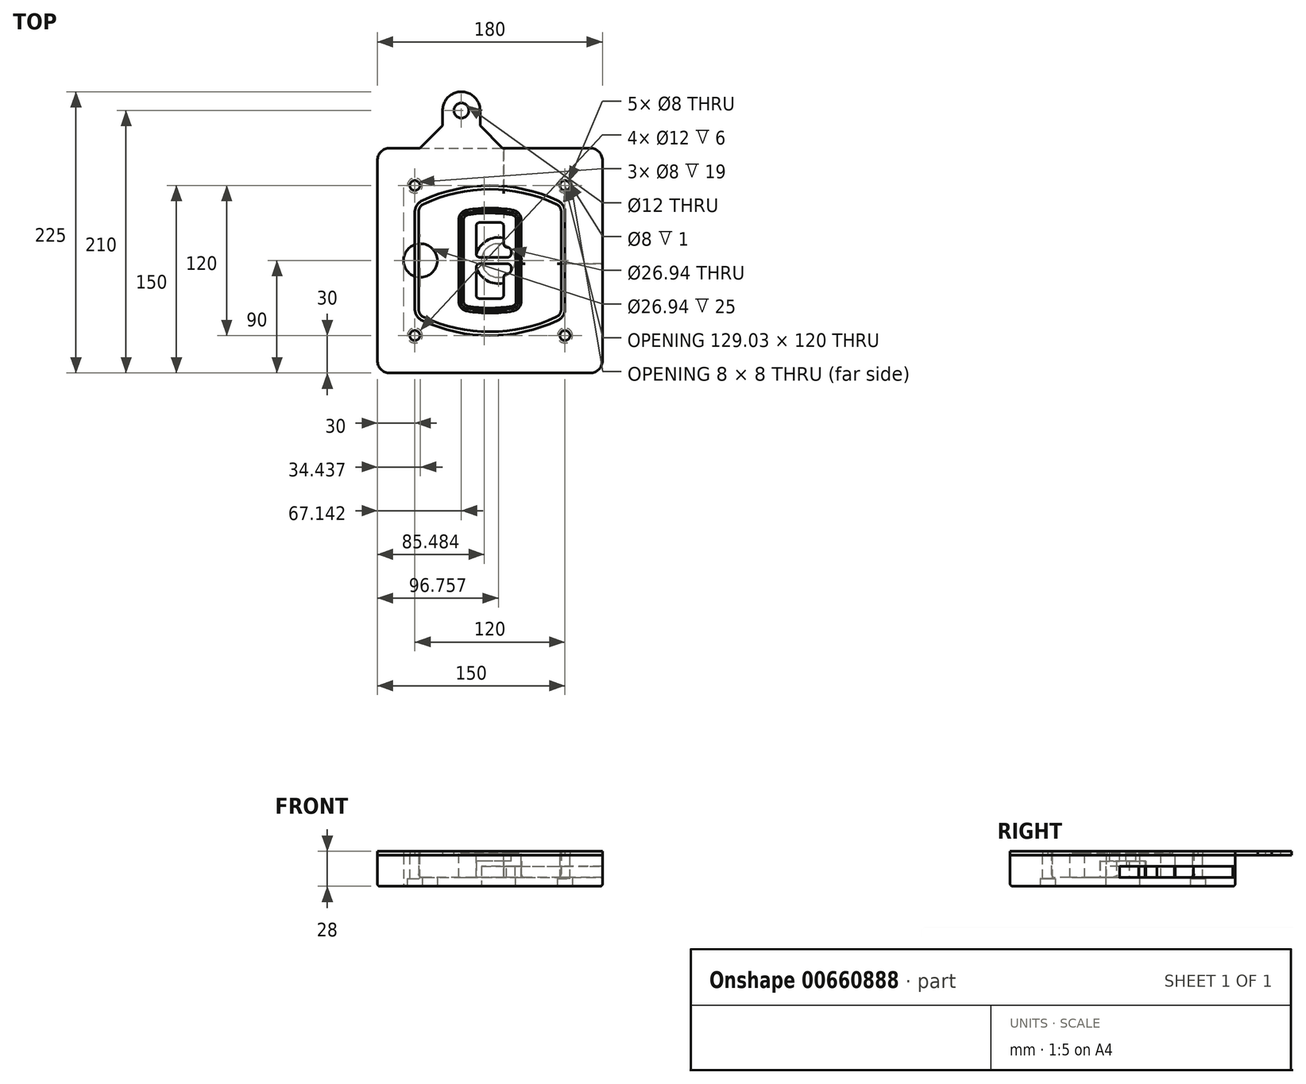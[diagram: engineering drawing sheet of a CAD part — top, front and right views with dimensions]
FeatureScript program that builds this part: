
annotation { "Feature Type Name" : "Feature", "Feature Type Description" : "" }
export const myFeature = defineFeature(function(context is Context, id is Id, definition is map)
    precondition{}
    {
        {
            var Q0;
            Q0=qCreatedBy(makeId("Top.planeOp"),FACE);
            var sketch = newSketch(context, id + "F0", { "sketchPlane" : qUnion([Q0])});
            skPoint(sketch, "E0.rect.middle", {"position": v(0, 0) * mm});
            skLineSegment(sketch, "E1.bottom", {"start": v(-80, -90) * mm, "end": v(80, -90) * mm});
            skLineSegment(sketch, "E1.top", {"start": v(-80, 90) * mm, "end": v(80, 90) * mm});
            skLineSegment(sketch, "E1.left", {"start": v(-90, -80) * mm, "end": v(-90, 80) * mm});
            skLineSegment(sketch, "E1.right", {"start": v(90, -80) * mm, "end": v(90, 80) * mm});
            skLineSegment(sketch, "E2", {"start": v(-90, 90) * mm, "end": v(90, -90) * mm, "construction": true});
            skLineSegment(sketch, "E3", {"start": v(90, 90) * mm, "end": v(-90, -90) * mm, "construction": true});
            skCircle(sketch, "E4", {"center": v(-60, 60) * mm, "radius": 4 * mm});
            skCircle(sketch, "E5", {"center": v(60, 60) * mm, "radius": 4 * mm});
            skCircle(sketch, "E6", {"center": v(60, -60) * mm, "radius": 4 * mm});
            skCircle(sketch, "E7", {"center": v(-60, -60) * mm, "radius": 4 * mm});
            skLineSegment(sketch, "E8", {"start": v(-60, 60) * mm, "end": v(60, 60) * mm, "construction": true});
            skLineSegment(sketch, "E9", {"start": v(60, 60) * mm, "end": v(60, -60) * mm, "construction": true});
            skLineSegment(sketch, "E10", {"start": v(60, -60) * mm, "end": v(-60, -60) * mm, "construction": true});
            skLineSegment(sketch, "E11", {"start": v(-60, -60) * mm, "end": v(-60, 60) * mm, "construction": true});
            skLineSegment(sketch, "E12", {"start": v(-60, 38.83) * mm, "end": v(-60, -38.83) * mm});
            skLineSegment(sketch, "E13", {"start": v(60, 38.83) * mm, "end": v(60, -38.83) * mm});
            skArc(sketch, "E14", {"start": v(54.26, 47.88) * mm, "mid": v(0, 60) * mm, "end": v(-54.26, 47.88) * mm});
            skArc(sketch, "E15", {"start": v(-54.26, -47.88) * mm, "mid": v(0, -60) * mm, "end": v(54.26, -47.88) * mm});
            skLineSegment(sketch, "E16", {"start": v(-60, 0) * mm, "end": v(60, 0) * mm, "construction": true});
            skPoint(sketch, "E17.visualSharp", {"position": v(-60, -45) * mm});
            skArc(sketch, "E17.filletArc", {"start": v(-60, -38.83) * mm, "mid": v(-58.44, -44.2) * mm, "end": v(-54.26, -47.88) * mm});
            skPoint(sketch, "E18.visualSharp", {"position": v(-60, 45) * mm});
            skArc(sketch, "E18.filletArc", {"start": v(-54.26, 47.88) * mm, "mid": v(-58.44, 44.2) * mm, "end": v(-60, 38.83) * mm});
            skPoint(sketch, "E19.visualSharp", {"position": v(60, 45) * mm});
            skArc(sketch, "E19.filletArc", {"start": v(60, 38.83) * mm, "mid": v(58.44, 44.2) * mm, "end": v(54.26, 47.88) * mm});
            skPoint(sketch, "E20.visualSharp", {"position": v(60, -45) * mm});
            skArc(sketch, "E20.filletArc", {"start": v(54.26, -47.88) * mm, "mid": v(58.44, -44.2) * mm, "end": v(60, -38.83) * mm});
            skPoint(sketch, "E21.visualSharp", {"position": v(-90, 90) * mm});
            skArc(sketch, "E21.filletArc", {"start": v(-80, 90) * mm, "mid": v(-87.07, 87.07) * mm, "end": v(-90, 80) * mm});
            skPoint(sketch, "E22.visualSharp", {"position": v(90, 90) * mm});
            skArc(sketch, "E22.filletArc", {"start": v(90, 80) * mm, "mid": v(87.07, 87.07) * mm, "end": v(80, 90) * mm});
            skPoint(sketch, "E23.visualSharp", {"position": v(90, -90) * mm});
            skArc(sketch, "E23.filletArc", {"start": v(80, -90) * mm, "mid": v(87.07, -87.07) * mm, "end": v(90, -80) * mm});
            skPoint(sketch, "E24.visualSharp", {"position": v(-90, -90) * mm});
            skArc(sketch, "E24.filletArc", {"start": v(-90, -80) * mm, "mid": v(-87.07, -87.07) * mm, "end": v(-80, -90) * mm});
            skArc(sketch, "E25.0", {"start": v(57, 38.83) * mm, "mid": v(55.9, 42.58) * mm, "end": v(52.98, 45.17) * mm});
            skLineSegment(sketch, "E25.1", {"start": v(57, 38.83) * mm, "end": v(57, -38.83) * mm});
            skArc(sketch, "E25.2", {"start": v(52.98, -45.17) * mm, "mid": v(55.9, -42.58) * mm, "end": v(57, -38.83) * mm});
            skArc(sketch, "E25.3", {"start": v(-52.98, -45.17) * mm, "mid": v(0, -57) * mm, "end": v(52.98, -45.17) * mm});
            skArc(sketch, "E25.4", {"start": v(-57, -38.83) * mm, "mid": v(-55.9, -42.58) * mm, "end": v(-52.98, -45.17) * mm});
            skArc(sketch, "E25.5", {"start": v(52.98, 45.17) * mm, "mid": v(0, 57) * mm, "end": v(-52.98, 45.17) * mm});
            skLineSegment(sketch, "E25.6", {"start": v(-57, 38.83) * mm, "end": v(-57, -38.83) * mm});
            skArc(sketch, "E25.7", {"start": v(-52.98, 45.17) * mm, "mid": v(-55.9, 42.58) * mm, "end": v(-57, 38.83) * mm});
            skArc(sketch, "E26.0", {"start": v(-55.96, 51.5) * mm, "mid": v(-61.82, 46.33) * mm, "end": v(-64, 38.83) * mm});
            skArc(sketch, "E26.1", {"start": v(55.96, 51.5) * mm, "mid": v(0, 64) * mm, "end": v(-55.96, 51.5) * mm});
            skArc(sketch, "E26.2", {"start": v(64, 38.83) * mm, "mid": v(61.82, 46.33) * mm, "end": v(55.96, 51.5) * mm});
            skLineSegment(sketch, "E26.3", {"start": v(64, 38.83) * mm, "end": v(64, -38.83) * mm});
            skArc(sketch, "E26.4", {"start": v(55.96, -51.5) * mm, "mid": v(61.82, -46.33) * mm, "end": v(64, -38.83) * mm});
            skLineSegment(sketch, "E26.5", {"start": v(-64, 38.83) * mm, "end": v(-64, -38.83) * mm});
            skArc(sketch, "E26.6", {"start": v(-55.96, -51.5) * mm, "mid": v(0, -64) * mm, "end": v(55.96, -51.5) * mm});
            skArc(sketch, "E26.7", {"start": v(-64, -38.83) * mm, "mid": v(-61.82, -46.33) * mm, "end": v(-55.96, -51.5) * mm});
            skSolve(sketch);
        }
        {
            var Q0;
            Q0=makeQuery(id+"F0.imprint","IMPRINT",FACE,{"disambiguationData":[TD([[makeQuery(id+"F0.imprint","IMPRINT",EDGE,{"derivedFrom":sQuery(id+"F0.wireOp",EDGE,"E1.bottom")}),1.0]])]});
            var Q1;
            Q1=makeQuery(id+"F0.imprint","IMPRINT",FACE,{"disambiguationData":[TD([[makeQuery(id+"F0.imprint","IMPRINT",EDGE,{"derivedFrom":sQuery(id+"F0.wireOp",EDGE,"E12")}),1.0]])]});
            var Q2;
            Q2=makeQuery(id+"F0.imprint","IMPRINT",FACE,{"disambiguationData":[TD([[makeQuery(id+"F0.imprint","IMPRINT",EDGE,{"derivedFrom":sQuery(id+"F0.wireOp",EDGE,"E25.0")}),1.0]])]});
            var Q3;
            Q3=makeQuery(id+"F0.imprint","IMPRINT",FACE,{"disambiguationData":[TD([[makeQuery(id+"F0.imprint","IMPRINT",EDGE,{"derivedFrom":sQuery(id+"F0.wireOp",EDGE,"E12")}),-1.0]])]});
            extrude(context, id + "F1", {"entities" : qUnion([Q0, Q1, Q2, Q3]), "oppositeDirection" : true, "depth" : 25 * mm});
        }
        {
            var Q0;
            Q0=makeQuery(id+"F0.imprint","IMPRINT",FACE,{"disambiguationData":[TD([[makeQuery(id+"F0.imprint","IMPRINT",EDGE,{"derivedFrom":sQuery(id+"F0.wireOp",EDGE,"E12")}),1.0]])]});
            extrude(context, id + "F2", {"entities" : qUnion([Q0]), "operationType" : NewBodyOperationType.ADD, "depth" : 3 * mm});
        }
        {
            var Q0;
            Q0=makeQuery(id+"F0.imprint","IMPRINT",FACE,{"disambiguationData":[TD([[makeQuery(id+"F0.imprint","IMPRINT",EDGE,{"derivedFrom":sQuery(id+"F0.wireOp",EDGE,"E25.0")}),1.0]])]});
            extrude(context, id + "F3", {"entities" : qUnion([Q0]), "operationType" : NewBodyOperationType.REMOVE, "oppositeDirection" : true, "depth" : 18 * mm});
        }
        {
            var Q0;
            Q0=makeQuery(id+"F2.opExtrude","CAP_FACE",FACE,{"disambiguationData":[OSD([sQuery(id+"F0.wireOp",EDGE,"E12"),sQuery(id+"F0.wireOp",EDGE,"E13"),sQuery(id+"F0.wireOp",EDGE,"E14"),sQuery(id+"F0.wireOp",EDGE,"E15"),sQuery(id+"F0.wireOp",EDGE,"E17.filletArc"),sQuery(id+"F0.wireOp",EDGE,"E18.filletArc"),sQuery(id+"F0.wireOp",EDGE,"E19.filletArc"),sQuery(id+"F0.wireOp",EDGE,"E20.filletArc"),sQuery(id+"F0.wireOp",EDGE,"E25.0"),sQuery(id+"F0.wireOp",EDGE,"E25.1"),sQuery(id+"F0.wireOp",EDGE,"E25.2"),sQuery(id+"F0.wireOp",EDGE,"E25.3"),sQuery(id+"F0.wireOp",EDGE,"E25.4"),sQuery(id+"F0.wireOp",EDGE,"E25.5"),sQuery(id+"F0.wireOp",EDGE,"E25.6"),sQuery(id+"F0.wireOp",EDGE,"E25.7")])],"isStart":false});
            var sketch = newSketch(context, id + "F4", { "sketchPlane" : qUnion([Q0])});
            skArc(sketch, "E27.0", {"start": v(-18.34, -40.45) * mm, "mid": v(0, -42) * mm, "end": v(18.34, -40.45) * mm});
            skArc(sketch, "E28.0", {"start": v(18.34, 40.45) * mm, "mid": v(0, 42) * mm, "end": v(-18.34, 40.45) * mm});
            skLineSegment(sketch, "E29", {"start": v(-25, 32.57) * mm, "end": v(-25, -32.57) * mm});
            skLineSegment(sketch, "E30", {"start": v(25, 32.57) * mm, "end": v(25, -32.57) * mm});
            skLineSegment(sketch, "E31", {"start": v(-25, 39.1) * mm, "end": v(25, 39.1) * mm, "construction": true});
            skLineSegment(sketch, "E32", {"start": v(-25, -39.1) * mm, "end": v(25, -39.1) * mm, "construction": true});
            skPoint(sketch, "E33.visualSharp", {"position": v(-25, 39.1) * mm});
            skArc(sketch, "E33.filletArc", {"start": v(-18.34, 40.45) * mm, "mid": v(-23.11, 37.73) * mm, "end": v(-25, 32.57) * mm});
            skPoint(sketch, "E34.visualSharp", {"position": v(25, 39.1) * mm});
            skArc(sketch, "E34.filletArc", {"start": v(25, 32.57) * mm, "mid": v(23.11, 37.73) * mm, "end": v(18.34, 40.45) * mm});
            skPoint(sketch, "E35.visualSharp", {"position": v(25, -39.1) * mm});
            skArc(sketch, "E35.filletArc", {"start": v(18.34, -40.45) * mm, "mid": v(23.11, -37.73) * mm, "end": v(25, -32.57) * mm});
            skPoint(sketch, "E36.visualSharp", {"position": v(-25, -39.1) * mm});
            skArc(sketch, "E36.filletArc", {"start": v(-25, -32.57) * mm, "mid": v(-23.11, -37.73) * mm, "end": v(-18.34, -40.45) * mm});
            skArc(sketch, "E37.0", {"start": v(52.98, 45.17) * mm, "mid": v(0, 57) * mm, "end": v(-52.98, 45.17) * mm});
            skArc(sketch, "E37.1", {"start": v(-52.98, 45.17) * mm, "mid": v(-55.9, 42.58) * mm, "end": v(-57, 38.83) * mm});
            skLineSegment(sketch, "E37.2", {"start": v(-57, 38.83) * mm, "end": v(-57, -38.83) * mm});
            skArc(sketch, "E37.3", {"start": v(-57, -38.83) * mm, "mid": v(-55.9, -42.58) * mm, "end": v(-52.98, -45.17) * mm});
            skArc(sketch, "E37.4", {"start": v(-52.98, -45.17) * mm, "mid": v(0, -57) * mm, "end": v(52.98, -45.17) * mm});
            skArc(sketch, "E37.5", {"start": v(52.98, -45.17) * mm, "mid": v(55.9, -42.58) * mm, "end": v(57, -38.83) * mm});
            skLineSegment(sketch, "E37.6", {"start": v(57, 38.83) * mm, "end": v(57, -38.83) * mm});
            skArc(sketch, "E37.7", {"start": v(57, 38.83) * mm, "mid": v(55.9, 42.58) * mm, "end": v(52.98, 45.17) * mm});
            skLineSegment(sketch, "E38.0", {"start": v(23, 32.57) * mm, "end": v(23, -32.57) * mm});
            skArc(sketch, "E38.1", {"start": v(18, -38.48) * mm, "mid": v(21.58, -36.44) * mm, "end": v(23, -32.57) * mm});
            skArc(sketch, "E38.2", {"start": v(-18, -38.48) * mm, "mid": v(0, -40) * mm, "end": v(18, -38.48) * mm});
            skArc(sketch, "E38.3", {"start": v(-23, -32.57) * mm, "mid": v(-21.58, -36.44) * mm, "end": v(-18, -38.48) * mm});
            skLineSegment(sketch, "E38.4", {"start": v(-23, 32.57) * mm, "end": v(-23, -32.57) * mm});
            skArc(sketch, "E38.5", {"start": v(23, 32.57) * mm, "mid": v(21.58, 36.44) * mm, "end": v(18, 38.48) * mm});
            skArc(sketch, "E38.6", {"start": v(-18, 38.48) * mm, "mid": v(-21.58, 36.44) * mm, "end": v(-23, 32.57) * mm});
            skArc(sketch, "E38.7", {"start": v(18, 38.48) * mm, "mid": v(0, 40) * mm, "end": v(-18, 38.48) * mm});
            skArc(sketch, "E39.0", {"start": v(21, 32.57) * mm, "mid": v(20.06, 35.15) * mm, "end": v(17.67, 36.5) * mm});
            skLineSegment(sketch, "E39.1", {"start": v(21, 32.57) * mm, "end": v(21, -32.57) * mm});
            skArc(sketch, "E39.2", {"start": v(17.67, -36.5) * mm, "mid": v(20.06, -35.15) * mm, "end": v(21, -32.57) * mm});
            skArc(sketch, "E39.3", {"start": v(-17.67, -36.5) * mm, "mid": v(0, -38) * mm, "end": v(17.67, -36.5) * mm});
            skArc(sketch, "E39.4", {"start": v(-21, -32.57) * mm, "mid": v(-20.06, -35.15) * mm, "end": v(-17.67, -36.5) * mm});
            skArc(sketch, "E39.5", {"start": v(17.67, 36.5) * mm, "mid": v(0, 38) * mm, "end": v(-17.67, 36.5) * mm});
            skLineSegment(sketch, "E39.6", {"start": v(-21, 32.57) * mm, "end": v(-21, -32.57) * mm});
            skArc(sketch, "E39.7", {"start": v(-17.67, 36.5) * mm, "mid": v(-20.06, 35.15) * mm, "end": v(-21, 32.57) * mm});
            skLineSegment(sketch, "E40", {"start": v(-25, 0) * mm, "end": v(25, 0) * mm, "construction": true});
            skLineSegment(sketch, "E41", {"start": v(-11, 5.5) * mm, "end": v(-11, 27.5) * mm});
            skLineSegment(sketch, "E42", {"start": v(-8, 30.5) * mm, "end": v(8, 30.5) * mm});
            skLineSegment(sketch, "E43", {"start": v(11, 27.5) * mm, "end": v(11, 13.5) * mm});
            skLineSegment(sketch, "E44", {"start": v(14, 10.5) * mm, "end": v(14, 10.5) * mm});
            skLineSegment(sketch, "E45", {"start": v(17, 7.5) * mm, "end": v(17, 5.5) * mm});
            skLineSegment(sketch, "E46", {"start": v(14, 2.5) * mm, "end": v(-8, 2.5) * mm});
            skPoint(sketch, "E47.visualSharp", {"position": v(-11, 30.5) * mm});
            skArc(sketch, "E47.filletArc", {"start": v(-8, 30.5) * mm, "mid": v(-10.12, 29.62) * mm, "end": v(-11, 27.5) * mm});
            skPoint(sketch, "E48.visualSharp", {"position": v(11, 30.5) * mm});
            skArc(sketch, "E48.filletArc", {"start": v(11, 27.5) * mm, "mid": v(10.12, 29.62) * mm, "end": v(8, 30.5) * mm});
            skPoint(sketch, "E49.visualSharp", {"position": v(11, 10.5) * mm});
            skArc(sketch, "E49.filletArc", {"start": v(11, 13.5) * mm, "mid": v(11.88, 11.38) * mm, "end": v(14, 10.5) * mm});
            skPoint(sketch, "E50.visualSharp", {"position": v(17, 10.5) * mm});
            skArc(sketch, "E50.filletArc", {"start": v(17, 7.5) * mm, "mid": v(16.12, 9.62) * mm, "end": v(14, 10.5) * mm});
            skPoint(sketch, "E51.visualSharp", {"position": v(17, 2.5) * mm});
            skArc(sketch, "E51.filletArc", {"start": v(14, 2.5) * mm, "mid": v(16.12, 3.38) * mm, "end": v(17, 5.5) * mm});
            skPoint(sketch, "E52.visualSharp", {"position": v(-11, 2.5) * mm});
            skArc(sketch, "E52.filletArc", {"start": v(-11, 5.5) * mm, "mid": v(-10.12, 3.38) * mm, "end": v(-8, 2.5) * mm});
            skLineSegment(sketch, "E53.0.MirrorCS", {"start": v(14, -2.5) * mm, "end": v(-8, -2.5) * mm});
            skArc(sketch, "E54.0.MirrorCS", {"start": v(-11, -5.5) * mm, "mid": v(-10.12, -3.38) * mm, "end": v(-8, -2.5) * mm});
            skLineSegment(sketch, "E55.0.MirrorCS", {"start": v(-11, -5.5) * mm, "end": v(-11, -27.5) * mm});
            skArc(sketch, "E56.0.MirrorCS", {"start": v(-8, -30.5) * mm, "mid": v(-10.12, -29.62) * mm, "end": v(-11, -27.5) * mm});
            skLineSegment(sketch, "E57.0.MirrorCS", {"start": v(-8, -30.5) * mm, "end": v(8, -30.5) * mm});
            skArc(sketch, "E58.0.MirrorCS", {"start": v(11, -27.5) * mm, "mid": v(10.12, -29.62) * mm, "end": v(8, -30.5) * mm});
            skLineSegment(sketch, "E59.0.MirrorCS", {"start": v(11, -27.5) * mm, "end": v(11, -13.5) * mm});
            skArc(sketch, "E60.0.MirrorCS", {"start": v(11, -13.5) * mm, "mid": v(11.88, -11.38) * mm, "end": v(14, -10.5) * mm});
            skArc(sketch, "E61.0.MirrorCS", {"start": v(17, -7.5) * mm, "mid": v(16.12, -9.62) * mm, "end": v(14, -10.5) * mm});
            skLineSegment(sketch, "E62.0.MirrorCS", {"start": v(17, -7.5) * mm, "end": v(17, -5.5) * mm});
            skArc(sketch, "E63.0.MirrorCS", {"start": v(14, -2.5) * mm, "mid": v(16.12, -3.38) * mm, "end": v(17, -5.5) * mm});
            skSolve(sketch);
        }
        {
            var Q0;
            Q0=makeQuery(id+"F4.imprint","IMPRINT",FACE,{"disambiguationData":[TD([[makeQuery(id+"F4.imprint","IMPRINT",EDGE,{"derivedFrom":sQuery(id+"F4.wireOp",EDGE,"E27.0")}),1.0]])]});
            var Q1;
            Q1=makeQuery(id+"F4.imprint","IMPRINT",FACE,{"disambiguationData":[TD([[makeQuery(id+"F4.imprint","IMPRINT",EDGE,{"derivedFrom":sQuery(id+"F4.wireOp",EDGE,"E38.0")}),-1.0]])]});
            var Q2;
            Q2=makeQuery(id+"F4.imprint","IMPRINT",FACE,{"disambiguationData":[TD([[makeQuery(id+"F4.imprint","IMPRINT",EDGE,{"derivedFrom":sQuery(id+"F4.wireOp",EDGE,"E39.0")}),1.0]])]});
            extrude(context, id + "F5", {"entities" : qUnion([Q0, Q1, Q2]), "operationType" : NewBodyOperationType.ADD, "endBound" : BoundingType.UP_TO_NEXT, "oppositeDirection" : true, "depth" : 25 * mm});
        }
        {
            var Q0;
            Q0=makeQuery(id+"F4.imprint","IMPRINT",FACE,{"disambiguationData":[TD([[makeQuery(id+"F4.imprint","IMPRINT",EDGE,{"derivedFrom":sQuery(id+"F4.wireOp",EDGE,"E38.0")}),-1.0]])]});
            extrude(context, id + "F6", {"entities" : qUnion([Q0]), "operationType" : NewBodyOperationType.REMOVE, "oppositeDirection" : true, "depth" : 2 * mm});
        }
        {
            var Q0;
            Q0=makeQuery(id+"F1.opExtrude","CAP_FACE",FACE,{"disambiguationData":[OSD([sQuery(id+"F0.wireOp",EDGE,"E1.bottom"),sQuery(id+"F0.wireOp",EDGE,"E1.top"),sQuery(id+"F0.wireOp",EDGE,"E1.left"),sQuery(id+"F0.wireOp",EDGE,"E1.right"),sQuery(id+"F0.wireOp",EDGE,"E4"),sQuery(id+"F0.wireOp",EDGE,"E5"),sQuery(id+"F0.wireOp",EDGE,"E6"),sQuery(id+"F0.wireOp",EDGE,"E7"),sQuery(id+"F0.wireOp",EDGE,"E21.filletArc"),sQuery(id+"F0.wireOp",EDGE,"E22.filletArc"),sQuery(id+"F0.wireOp",EDGE,"E23.filletArc"),sQuery(id+"F0.wireOp",EDGE,"E24.filletArc")])],"isStart":false});
            var sketch = newSketch(context, id + "F7", { "sketchPlane" : qUnion([Q0])});
            skCircle(sketch, "E64", {"center": v(6.76, 0) * mm, "radius": 13.47 * mm});
            skCircle(sketch, "E65", {"center": v(-55.56, 0) * mm, "radius": 13.47 * mm});
            skLineSegment(sketch, "E66", {"start": v(90, 0) * mm, "end": v(-90, 0) * mm});
            skCircle(sketch, "E67", {"center": v(6.76, 0) * mm, "radius": 18.47 * mm});
            skCircle(sketch, "E68", {"center": v(60, -60) * mm, "radius": 6 * mm});
            skCircle(sketch, "E69", {"center": v(-60, -60) * mm, "radius": 6 * mm});
            skCircle(sketch, "E70", {"center": v(-60, 60) * mm, "radius": 6 * mm});
            skCircle(sketch, "E71", {"center": v(60, 60) * mm, "radius": 6 * mm});
            skSolve(sketch);
        }
        {
            var Q0;
            {var subQ1=sQuery(id+"F7.wireOp",EDGE,"E66");var subQ4=sQuery(id+"F7.wireOp",EDGE,"E64");var subQ6=makeQuery(id+"F7.imprint","INTERSECT",VERTEX,{"disambiguationData":[OD(0.0)],"derivedFrom":[subQ4,subQ1]});Q0=makeQuery(id+"F7.imprint","IMPRINT",FACE,{"disambiguationData":[TD([[makeQuery(id+"F7.imprint","IMPRINT",EDGE,{"disambiguationData":[TD([[subQ6,-1.0]])],"derivedFrom":subQ4}),-1.0]])]});}
            var Q1;
            {var subQ0=sQuery(id+"F7.wireOp",EDGE,"E66");var subQ1=sQuery(id+"F7.wireOp",EDGE,"E64");var subQ3=makeQuery(id+"F7.imprint","INTERSECT",VERTEX,{"disambiguationData":[OD(0.0)],"derivedFrom":[subQ1,subQ0]});Q1=makeQuery(id+"F7.imprint","IMPRINT",FACE,{"disambiguationData":[TD([[makeQuery(id+"F7.imprint","IMPRINT",EDGE,{"disambiguationData":[TD([[subQ3,-1.0]])],"derivedFrom":subQ1}),1.0]])]});}
            var Q2;
            {var subQ0=sQuery(id+"F7.wireOp",EDGE,"E66");var subQ1=sQuery(id+"F7.wireOp",EDGE,"E64");var subQ3=makeQuery(id+"F7.imprint","INTERSECT",VERTEX,{"disambiguationData":[OD(0.0)],"derivedFrom":[subQ1,subQ0]});Q2=makeQuery(id+"F7.imprint","IMPRINT",FACE,{"disambiguationData":[TD([[makeQuery(id+"F7.imprint","IMPRINT",EDGE,{"disambiguationData":[TD([[subQ3,1.0]])],"derivedFrom":subQ1}),1.0]])]});}
            var Q3;
            {var subQ1=sQuery(id+"F7.wireOp",EDGE,"E66");var subQ4=sQuery(id+"F7.wireOp",EDGE,"E64");var subQ6=makeQuery(id+"F7.imprint","INTERSECT",VERTEX,{"disambiguationData":[OD(0.0)],"derivedFrom":[subQ4,subQ1]});Q3=makeQuery(id+"F7.imprint","IMPRINT",FACE,{"disambiguationData":[TD([[makeQuery(id+"F7.imprint","IMPRINT",EDGE,{"disambiguationData":[TD([[subQ6,1.0]])],"derivedFrom":subQ4}),-1.0]])]});}
            extrude(context, id + "F8", {"entities" : qUnion([Q0, Q1, Q2, Q3]), "operationType" : NewBodyOperationType.ADD, "oppositeDirection" : true, "depth" : 20 * mm});
        }
        {
            var Q0;
            {var subQ0=sQuery(id+"F7.wireOp",EDGE,"E66");var subQ1=sQuery(id+"F7.wireOp",EDGE,"E64");var subQ3=makeQuery(id+"F7.imprint","INTERSECT",VERTEX,{"disambiguationData":[OD(0.0)],"derivedFrom":[subQ1,subQ0]});Q0=makeQuery(id+"F7.imprint","IMPRINT",FACE,{"disambiguationData":[TD([[makeQuery(id+"F7.imprint","IMPRINT",EDGE,{"disambiguationData":[TD([[subQ3,-1.0]])],"derivedFrom":subQ1}),1.0]])]});}
            var Q1;
            {var subQ0=sQuery(id+"F7.wireOp",EDGE,"E66");var subQ1=sQuery(id+"F7.wireOp",EDGE,"E64");var subQ3=makeQuery(id+"F7.imprint","INTERSECT",VERTEX,{"disambiguationData":[OD(0.0)],"derivedFrom":[subQ1,subQ0]});Q1=makeQuery(id+"F7.imprint","IMPRINT",FACE,{"disambiguationData":[TD([[makeQuery(id+"F7.imprint","IMPRINT",EDGE,{"disambiguationData":[TD([[subQ3,1.0]])],"derivedFrom":subQ1}),1.0]])]});}
            extrude(context, id + "F9", {"entities" : qUnion([Q0, Q1]), "operationType" : NewBodyOperationType.REMOVE, "oppositeDirection" : true, "depth" : 16 * mm});
        }
        {
            var Q0;
            {var subQ0=sQuery(id+"F7.wireOp",EDGE,"E66");var subQ1=sQuery(id+"F7.wireOp",EDGE,"E65");var subQ3=makeQuery(id+"F7.imprint","INTERSECT",VERTEX,{"disambiguationData":[OD(0.0)],"derivedFrom":[subQ1,subQ0]});Q0=makeQuery(id+"F7.imprint","IMPRINT",FACE,{"disambiguationData":[TD([[makeQuery(id+"F7.imprint","IMPRINT",EDGE,{"disambiguationData":[TD([[subQ3,-1.0]])],"derivedFrom":subQ1}),1.0]])]});}
            var Q1;
            {var subQ0=sQuery(id+"F7.wireOp",EDGE,"E66");var subQ1=sQuery(id+"F7.wireOp",EDGE,"E65");var subQ3=makeQuery(id+"F7.imprint","INTERSECT",VERTEX,{"disambiguationData":[OD(0.0)],"derivedFrom":[subQ1,subQ0]});Q1=makeQuery(id+"F7.imprint","IMPRINT",FACE,{"disambiguationData":[TD([[makeQuery(id+"F7.imprint","IMPRINT",EDGE,{"disambiguationData":[TD([[subQ3,1.0]])],"derivedFrom":subQ1}),1.0]])]});}
            extrude(context, id + "F10", {"entities" : qUnion([Q0, Q1]), "operationType" : NewBodyOperationType.REMOVE, "oppositeDirection" : true, "depth" : 25 * mm});
        }
        {
            var Q0;
            Q0=makeQuery(id+"F7.imprint","IMPRINT",FACE,{"disambiguationData":[TD([[makeQuery(id+"F7.imprint","IMPRINT",EDGE,{"derivedFrom":sQuery(id+"F7.wireOp",EDGE,"E68")}),1.0]])]});
            var Q1;
            Q1=makeQuery(id+"F7.imprint","IMPRINT",FACE,{"disambiguationData":[TD([[makeQuery(id+"F7.imprint","IMPRINT",EDGE,{"derivedFrom":makeQuery(id+"F1.opExtrude","CAP_EDGE",EDGE,{"disambiguationData":[OSD([sQuery(id+"F0.wireOp",EDGE,"E5")])],"isStart":false})}),-1.0]])]});
            var Q2;
            Q2=makeQuery(id+"F7.imprint","IMPRINT",FACE,{"disambiguationData":[TD([[makeQuery(id+"F7.imprint","IMPRINT",EDGE,{"derivedFrom":sQuery(id+"F7.wireOp",EDGE,"E69")}),1.0]])]});
            var Q3;
            Q3=makeQuery(id+"F7.imprint","IMPRINT",FACE,{"disambiguationData":[TD([[makeQuery(id+"F7.imprint","IMPRINT",EDGE,{"derivedFrom":makeQuery(id+"F1.opExtrude","CAP_EDGE",EDGE,{"disambiguationData":[OSD([sQuery(id+"F0.wireOp",EDGE,"E4")])],"isStart":false})}),-1.0]])]});
            var Q4;
            Q4=makeQuery(id+"F7.imprint","IMPRINT",FACE,{"disambiguationData":[TD([[makeQuery(id+"F7.imprint","IMPRINT",EDGE,{"derivedFrom":sQuery(id+"F7.wireOp",EDGE,"E70")}),1.0]])]});
            var Q5;
            Q5=makeQuery(id+"F7.imprint","IMPRINT",FACE,{"disambiguationData":[TD([[makeQuery(id+"F7.imprint","IMPRINT",EDGE,{"derivedFrom":makeQuery(id+"F1.opExtrude","CAP_EDGE",EDGE,{"disambiguationData":[OSD([sQuery(id+"F0.wireOp",EDGE,"E7")])],"isStart":false})}),-1.0]])]});
            var Q6;
            Q6=makeQuery(id+"F7.imprint","IMPRINT",FACE,{"disambiguationData":[TD([[makeQuery(id+"F7.imprint","IMPRINT",EDGE,{"derivedFrom":sQuery(id+"F7.wireOp",EDGE,"E71")}),1.0]])]});
            var Q7;
            Q7=makeQuery(id+"F7.imprint","IMPRINT",FACE,{"disambiguationData":[TD([[makeQuery(id+"F7.imprint","IMPRINT",EDGE,{"derivedFrom":makeQuery(id+"F1.opExtrude","CAP_EDGE",EDGE,{"disambiguationData":[OSD([sQuery(id+"F0.wireOp",EDGE,"E6")])],"isStart":false})}),-1.0]])]});
            extrude(context, id + "F11", {"entities" : qUnion([Q0, Q1, Q2, Q3, Q4, Q5, Q6, Q7]), "operationType" : NewBodyOperationType.REMOVE, "oppositeDirection" : true, "depth" : 6 * mm});
        }
        {
            var Q0;
            Q0=makeQuery(id+"F9.boolean.opBoolean","COPY",FACE,{"derivedFrom":makeQuery(id+"F9.opExtrude","CAP_FACE",FACE,{"disambiguationData":[OSD([sQuery(id+"F7.wireOp",EDGE,"E64")])],"isStart":false})});
            var sketch = newSketch(context, id + "F12", { "sketchPlane" : qUnion([Q0])});
            skArc(sketch, "E72.0", {"start": v(11, -88.19) * mm, "mid": v(97.1, -83.6) * mm, "end": v(92.5, 2.5) * mm});
            skLineSegment(sketch, "E72.1", {"start": v(11, -17.97) * mm, "end": v(11, -17.97) * mm});
            skLineSegment(sketch, "E73", {"start": v(92.5, -105.13) * mm, "end": v(102.3, -105.13) * mm});
            skLineSegment(sketch, "E74.0", {"start": v(92.5, 2.5) * mm, "end": v(14, 2.5) * mm});
            skArc(sketch, "E74.1", {"start": v(14, 2.5) * mm, "mid": v(16.12, 3.38) * mm, "end": v(17, 5.5) * mm});
            skLineSegment(sketch, "E74.2", {"start": v(17, 7.5) * mm, "end": v(17, 5.5) * mm});
            skArc(sketch, "E74.3", {"start": v(17, 7.5) * mm, "mid": v(16.12, 9.62) * mm, "end": v(14, 10.5) * mm});
            skArc(sketch, "E74.4", {"start": v(11, 13.5) * mm, "mid": v(11.88, 11.38) * mm, "end": v(14, 10.5) * mm});
            skLineSegment(sketch, "E74.5", {"start": v(11, 13.5) * mm, "end": v(11, -88.19) * mm});
            skLineSegment(sketch, "E74.7", {"start": v(92.5, -2.5) * mm, "end": v(14, -2.5) * mm});
            skArc(sketch, "E74.8", {"start": v(14, -2.5) * mm, "mid": v(16.12, -3.38) * mm, "end": v(17, -5.5) * mm});
            skLineSegment(sketch, "E74.9", {"start": v(17, -7.5) * mm, "end": v(17, -5.5) * mm});
            skArc(sketch, "E74.10", {"start": v(17, -7.5) * mm, "mid": v(16.12, -9.62) * mm, "end": v(14, -10.5) * mm});
            skArc(sketch, "E74.11", {"start": v(11, -13.5) * mm, "mid": v(11.88, -11.38) * mm, "end": v(14, -10.5) * mm});
            skLineSegment(sketch, "E74.12", {"start": v(11, -17.97) * mm, "end": v(11, -13.5) * mm});
            skPoint(sketch, "E75.orphan", {"position": v(11, -27.5) * mm});
            skPoint(sketch, "E76.orphan", {"position": v(-8, -2.5) * mm});
            skPoint(sketch, "E77.orphan", {"position": v(-8, 2.5) * mm});
            skPoint(sketch, "E78.orphan", {"position": v(11, 27.5) * mm});
            skSolve(sketch);
        }
        {
            var Q0;
            {var subQ7=sQuery(id+"F12.wireOp",EDGE,"E72.0");var subQ14=sQuery(id+"F12.wireOp",EDGE,"E72.1");var subQ16=sQuery(id+"F12.wireOp",EDGE,"E74.1");var subQ18=sQuery(id+"F12.wireOp",EDGE,"E74.8");Q0=qUnion([makeQuery(id+"F12.imprint","IMPRINT",FACE,{"disambiguationData":[TD([[makeQuery(id+"F12.imprint","IMPRINT",EDGE,{"derivedFrom":subQ7}),1.0]])]}),makeQuery(id+"F12.imprint","IMPRINT",FACE,{"disambiguationData":[TD([[makeQuery(id+"F12.imprint","IMPRINT",EDGE,{"derivedFrom":subQ14}),1.0]])]}),makeQuery(id+"F12.imprint","IMPRINT",FACE,{"disambiguationData":[TD([[makeQuery(id+"F12.imprint","IMPRINT",EDGE,{"derivedFrom":subQ16}),1.0]])]}),makeQuery(id+"F12.imprint","IMPRINT",FACE,{"disambiguationData":[TD([[makeQuery(id+"F12.imprint","IMPRINT",EDGE,{"derivedFrom":subQ18}),-1.0]])]})]);}
            var Q1;
            Q1=makeQuery(id+"F5.boolean.opBoolean","SPLIT",FACE,{"disambiguationData":[TD([makeQuery(id+"F5.opExtrude","SWEPT_FACE",FACE,{"disambiguationData":[OSD([sQuery(id+"F4.wireOp",EDGE,"E41")])]})])],"derivedFrom":makeQuery(id+"F3.boolean.opBoolean","COPY",FACE,{"derivedFrom":makeQuery(id+"F3.opExtrude","CAP_FACE",FACE,{"disambiguationData":[OSD([sQuery(id+"F0.wireOp",EDGE,"E25.0"),sQuery(id+"F0.wireOp",EDGE,"E25.1"),sQuery(id+"F0.wireOp",EDGE,"E25.2"),sQuery(id+"F0.wireOp",EDGE,"E25.3"),sQuery(id+"F0.wireOp",EDGE,"E25.4"),sQuery(id+"F0.wireOp",EDGE,"E25.5"),sQuery(id+"F0.wireOp",EDGE,"E25.6"),sQuery(id+"F0.wireOp",EDGE,"E25.7")])],"isStart":false})})});
            extrude(context, id + "F13", {"entities" : qUnion([Q0]), "operationType" : NewBodyOperationType.REMOVE, "endBound" : BoundingType.UP_TO_SURFACE, "endBoundEntityFace" : qUnion([Q1]), "depth" : 25 * mm});
        }
        {
            var Q0;
            Q0=makeQuery(id+"F3.boolean.opBoolean","COPY",EDGE,{"derivedFrom":makeQuery(id+"F3.opExtrude","CAP_EDGE",EDGE,{"disambiguationData":[OSD([sQuery(id+"F0.wireOp",EDGE,"E25.6")])],"isStart":false})});
            var Q1;
            Q1=makeQuery(id+"F8.boolean.opBoolean","INTERSECT",EDGE,{"derivedFrom":[makeQuery(id+"F5.opExtrude","SWEPT_FACE",FACE,{"disambiguationData":[OSD([sQuery(id+"F4.wireOp",EDGE,"E30")])]}),makeQuery(id+"F8.opExtrude","CAP_FACE",FACE,{"disambiguationData":[OSD([sQuery(id+"F7.wireOp",EDGE,"E67")])],"isStart":false})]});
            var Q2;
            Q2=makeQuery(id+"F8.boolean.opBoolean","INTERSECT",EDGE,{"disambiguationData":[OD(1.0)],"derivedFrom":[makeQuery(id+"F5.opExtrude","SWEPT_FACE",FACE,{"disambiguationData":[OSD([sQuery(id+"F4.wireOp",EDGE,"E30")])]}),makeQuery(id+"F8.opExtrude","SWEPT_FACE",FACE,{"disambiguationData":[OSD([sQuery(id+"F7.wireOp",EDGE,"E67")])]})]});
            var Q3;
            {var subQ0=makeQuery(id+"F3.boolean.opBoolean","COPY",FACE,{"derivedFrom":makeQuery(id+"F3.opExtrude","CAP_FACE",FACE,{"disambiguationData":[OSD([sQuery(id+"F0.wireOp",EDGE,"E25.0"),sQuery(id+"F0.wireOp",EDGE,"E25.1"),sQuery(id+"F0.wireOp",EDGE,"E25.2"),sQuery(id+"F0.wireOp",EDGE,"E25.3"),sQuery(id+"F0.wireOp",EDGE,"E25.4"),sQuery(id+"F0.wireOp",EDGE,"E25.5"),sQuery(id+"F0.wireOp",EDGE,"E25.6"),sQuery(id+"F0.wireOp",EDGE,"E25.7")])],"isStart":false})});var subQ1=sQuery(id+"F4.wireOp",EDGE,"E30");Q3=makeQuery(id+"F8.boolean.opBoolean","SPLIT",EDGE,{"disambiguationData":[TD([makeQuery(id+"F5.opExtrude","SWEPT_FACE",FACE,{"disambiguationData":[OSD([sQuery(id+"F4.wireOp",EDGE,"E35.filletArc")])]})])],"derivedFrom":makeQuery(id+"F5.opExtrude","TWEAK_EDGE",EDGE,{"derivedFrom":[subQ0,makeQuery(id+"F4.imprint","IMPRINT",EDGE,{"derivedFrom":subQ1})]})});}
            var Q4;
            {var subQ0=sQuery(id+"F0.wireOp",EDGE,"E25.0");var subQ1=sQuery(id+"F0.wireOp",EDGE,"E25.1");var subQ2=sQuery(id+"F0.wireOp",EDGE,"E25.2");var subQ3=sQuery(id+"F0.wireOp",EDGE,"E25.3");var subQ4=sQuery(id+"F0.wireOp",EDGE,"E25.4");var subQ5=sQuery(id+"F0.wireOp",EDGE,"E25.5");var subQ6=sQuery(id+"F0.wireOp",EDGE,"E25.6");var subQ7=sQuery(id+"F0.wireOp",EDGE,"E25.7");Q4=makeQuery(id+"F8.boolean.opBoolean","INTERSECT",EDGE,{"derivedFrom":[makeQuery(id+"F5.boolean.opBoolean","SPLIT",FACE,{"disambiguationData":[TD([makeQuery(id+"F2.opExtrude","SWEPT_FACE",FACE,{"disambiguationData":[OSD([subQ0])]})])],"derivedFrom":makeQuery(id+"F3.boolean.opBoolean","COPY",FACE,{"derivedFrom":makeQuery(id+"F3.opExtrude","CAP_FACE",FACE,{"disambiguationData":[OSD([subQ0,subQ1,subQ2,subQ3,subQ4,subQ5,subQ6,subQ7])],"isStart":false})})}),makeQuery(id+"F8.opExtrude","SWEPT_FACE",FACE,{"disambiguationData":[OSD([sQuery(id+"F7.wireOp",EDGE,"E67")])]})]});}
            var Q5;
            Q5=makeQuery(id+"F8.boolean.opBoolean","INTERSECT",EDGE,{"disambiguationData":[OD(0.0)],"derivedFrom":[makeQuery(id+"F5.opExtrude","SWEPT_FACE",FACE,{"disambiguationData":[OSD([sQuery(id+"F4.wireOp",EDGE,"E30")])]}),makeQuery(id+"F8.opExtrude","SWEPT_FACE",FACE,{"disambiguationData":[OSD([sQuery(id+"F7.wireOp",EDGE,"E67")])]})]});
            fillet(context, id + "F14", {"entities" : qUnion([Q0, Q1, Q2, Q3, Q4, Q5]), "radius" : 3 * mm, "tangentPropagation" : true, "allowEdgeOverflow" : false});
        }
        {
            var Q0;
            Q0=makeQuery(id+"F1.opExtrude","CAP_EDGE",EDGE,{"disambiguationData":[OSD([sQuery(id+"F0.wireOp",EDGE,"E1.bottom")])],"isStart":false});
            fillet(context, id + "F15", {"entities" : qUnion([Q0]), "radius" : 2 * mm, "tangentPropagation" : true, "allowEdgeOverflow" : false});
        }
        {
            var Q0;
            {var subQ0=sQuery(id+"F0.wireOp",EDGE,"E21.filletArc");var subQ1=sQuery(id+"F0.wireOp",EDGE,"E7");var subQ2=sQuery(id+"F0.wireOp",EDGE,"E6");var subQ3=sQuery(id+"F0.wireOp",EDGE,"E5");var subQ4=sQuery(id+"F0.wireOp",EDGE,"E4");var subQ5=sQuery(id+"F0.wireOp",EDGE,"E22.filletArc");var subQ6=sQuery(id+"F0.wireOp",EDGE,"E1.bottom");var subQ7=sQuery(id+"F0.wireOp",EDGE,"E1.right");var subQ8=sQuery(id+"F0.wireOp",EDGE,"E1.top");var subQ9=sQuery(id+"F0.wireOp",EDGE,"E1.left");var subQ10=sQuery(id+"F0.wireOp",EDGE,"E23.filletArc");var subQ11=sQuery(id+"F0.wireOp",EDGE,"E24.filletArc");Q0=makeQuery(id+"F2.boolean.opBoolean","SPLIT",FACE,{"disambiguationData":[TD([makeQuery(id+"F1.opExtrude","SWEPT_FACE",FACE,{"disambiguationData":[OSD([subQ6])]})])],"derivedFrom":makeQuery(id+"F1.opExtrude","CAP_FACE",FACE,{"disambiguationData":[OSD([subQ6,subQ8,subQ9,subQ7,subQ4,subQ3,subQ2,subQ1,subQ0,subQ5,subQ10,subQ11])],"isStart":true})});}
            var sketch = newSketch(context, id + "F16", { "sketchPlane" : qUnion([Q0])});
            skLineSegment(sketch, "E79", {"start": v(-55.86, 90) * mm, "end": v(-37.86, 108) * mm});
            skLineSegment(sketch, "E80", {"start": v(10.12, 90) * mm, "end": v(-7.88, 108) * mm});
            skLineSegment(sketch, "E81", {"start": v(-37.86, 108) * mm, "end": v(-37.86, 120) * mm});
            skLineSegment(sketch, "E82", {"start": v(-7.88, 108) * mm, "end": v(-7.88, 119.17) * mm});
            skArc(sketch, "E83", {"start": v(-7.88, 119.17) * mm, "mid": v(-22.44, 135) * mm, "end": v(-37.86, 120) * mm});
            skCircle(sketch, "E84", {"center": v(-22.86, 120) * mm, "radius": 6 * mm});
            skLineSegment(sketch, "E85", {"start": v(-22.86, 120) * mm, "end": v(-22.86, 90) * mm, "construction": true});
            skArc(sketch, "E86.MirrorCS", {"start": v(-7.88, -119.17) * mm, "mid": v(-22.44, -135) * mm, "end": v(-37.86, -120) * mm});
            skLineSegment(sketch, "E87.MirrorCS", {"start": v(10.12, -90) * mm, "end": v(-7.88, -108) * mm});
            skLineSegment(sketch, "E88.MirrorCS", {"start": v(-7.88, -108) * mm, "end": v(-7.88, -119.17) * mm});
            skLineSegment(sketch, "E89.MirrorCS", {"start": v(-37.86, -108) * mm, "end": v(-37.86, -120) * mm});
            skLineSegment(sketch, "E90.MirrorCS", {"start": v(-55.86, -90) * mm, "end": v(-37.86, -108) * mm});
            skLineSegment(sketch, "E91.MirrorCS", {"start": v(-22.86, -120) * mm, "end": v(-22.86, -90) * mm, "construction": true});
            skCircle(sketch, "E92.MirrorC", {"center": v(-22.86, -120) * mm, "radius": 6 * mm});
            skText(sketch, "E93", { "text": "Cabrera Volume: 65,008.297 mm cubed ", "fontName": "OpenSans-Regular.ttf"});
            const initialGuessF16  = {"E93": [0.02412, 0.11516, 1, 0, 0.03882]};
            skSetInitialGuess(sketch, initialGuessF16);
            skSolve(sketch);
        }
        {
            var Q0;
            Q0=makeQuery(id+"F16.imprint","IMPRINT",FACE,{"disambiguationData":[TD([[makeQuery(id+"F16.imprint","IMPRINT",EDGE,{"derivedFrom":sQuery(id+"F16.wireOp",EDGE,"E86.MirrorCS")}),-1.0]])]});
            var Q1;
            {var subQ0=sQuery(id+"F16.wireOp",EDGE,"E79");Q1=makeQuery(id+"F16.imprint","IMPRINT",FACE,{"disambiguationData":[TD([[makeQuery(id+"F16.imprint","IMPRINT",EDGE,{"derivedFrom":subQ0}),-1.0]])]});}
            var Q2;
            Q2=makeQuery(id+"F16.imprint","IMPRINT",FACE,{"disambiguationData":[TD([[makeQuery(id+"F16.imprint","IMPRINT",EDGE,{"derivedFrom":makeQuery(id+"F1.opExtrude","CAP_EDGE",EDGE,{"disambiguationData":[OSD([sQuery(id+"F0.wireOp",EDGE,"E1.left")])],"isStart":true})}),-1.0]])]});
            var Q3;
            Q3=makeQuery(id+"F2.opExtrude","CAP_FACE",FACE,{"disambiguationData":[OSD([sQuery(id+"F0.wireOp",EDGE,"E12"),sQuery(id+"F0.wireOp",EDGE,"E13"),sQuery(id+"F0.wireOp",EDGE,"E14"),sQuery(id+"F0.wireOp",EDGE,"E15"),sQuery(id+"F0.wireOp",EDGE,"E17.filletArc"),sQuery(id+"F0.wireOp",EDGE,"E18.filletArc"),sQuery(id+"F0.wireOp",EDGE,"E19.filletArc"),sQuery(id+"F0.wireOp",EDGE,"E20.filletArc"),sQuery(id+"F0.wireOp",EDGE,"E25.0"),sQuery(id+"F0.wireOp",EDGE,"E25.1"),sQuery(id+"F0.wireOp",EDGE,"E25.2"),sQuery(id+"F0.wireOp",EDGE,"E25.3"),sQuery(id+"F0.wireOp",EDGE,"E25.4"),sQuery(id+"F0.wireOp",EDGE,"E25.5"),sQuery(id+"F0.wireOp",EDGE,"E25.6"),sQuery(id+"F0.wireOp",EDGE,"E25.7")])],"isStart":false});
            extrude(context, id + "F17", {"entities" : qUnion([Q0, Q1, Q2]), "endBound" : BoundingType.UP_TO_SURFACE, "depth" : 25.4 * mm, "endBoundEntityFace" : qUnion([Q3]), "offsetDistance" : 25.4 * mm});
        }
    });
